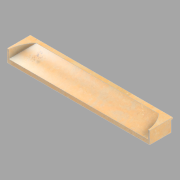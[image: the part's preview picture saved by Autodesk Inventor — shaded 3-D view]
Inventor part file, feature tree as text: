
AUTODESK INVENTOR PART (.ipt)
format: ipt  version: 2022.2 (Build 262287010, 287A)  size: 136,704 bytes
history: native  units: in
note: dims shown in document units (in); Inventor stores cm internally (conversion verified against a paired STEP export)
features: other x1, direct_edit x1, revolve x1
ambient origin geometry x8: Origin, YZ Plane, XZ Plane, XY Plane, X Axis, Y Axis, Z Axis, Center Point
bodies: Solid1 (feature_tree)
feature tree (3):
  other  "North (4) (3)"
  direct_edit  "Direct Edit1"
  revolve  "Rotate1"  Angle=90.0deg
